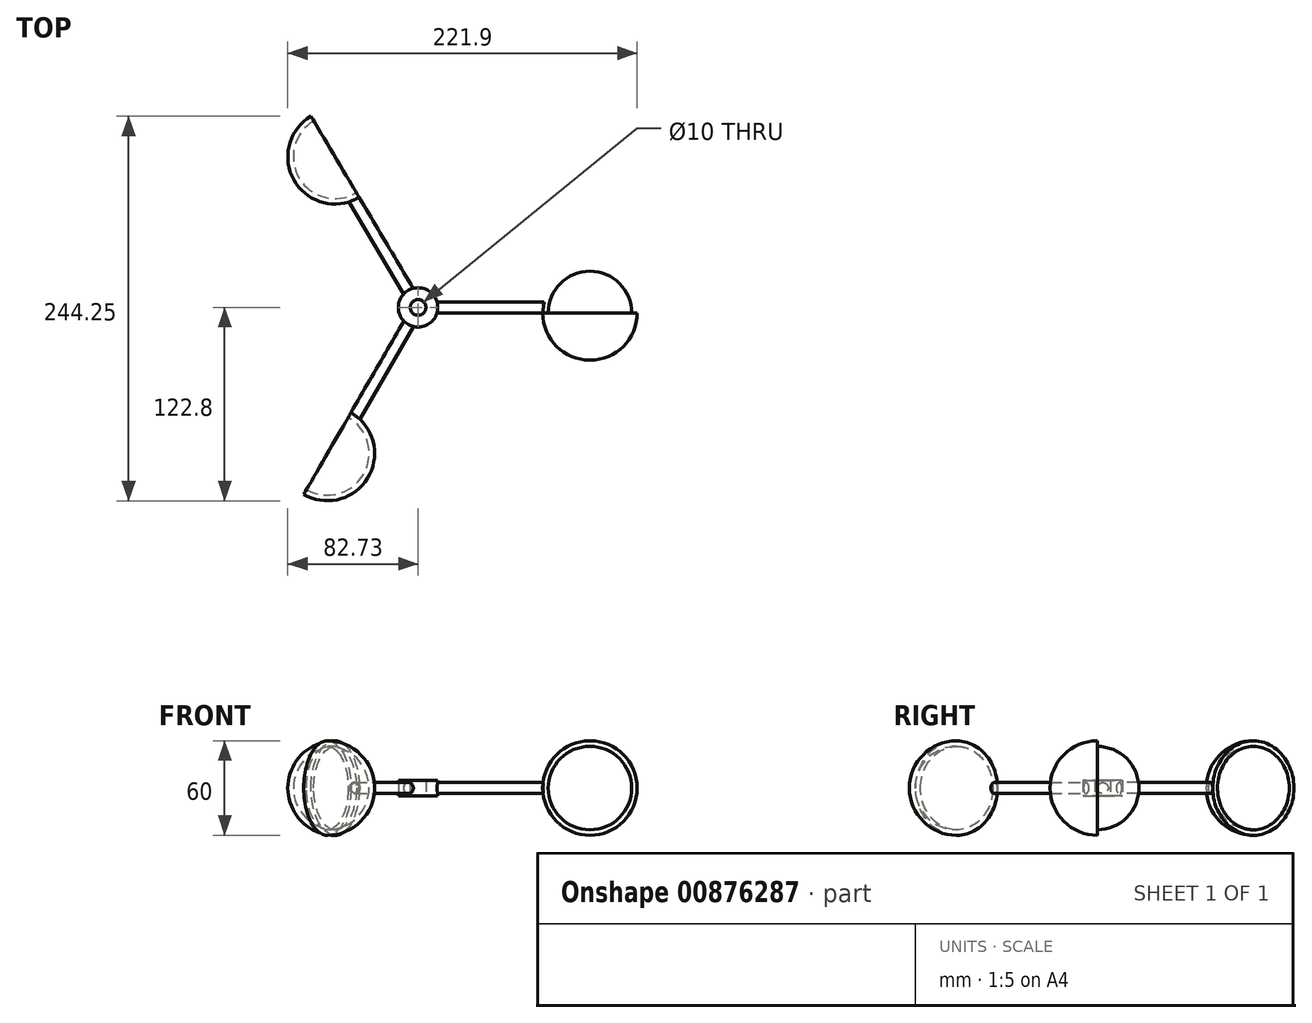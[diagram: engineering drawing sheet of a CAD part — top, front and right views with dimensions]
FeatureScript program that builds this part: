
annotation { "Feature Type Name" : "Feature", "Feature Type Description" : "" }
export const myFeature = defineFeature(function(context is Context, id is Id, definition is map)
    precondition{}
    {
        {
            var Q0;
            Q0=qCreatedBy(makeId("Top.planeOp"),FACE);
            var sketch = newSketch(context, id + "F0", { "sketchPlane" : qUnion([Q0])});
            skCircle(sketch, "E0", {"center": v(0, 0) * mm, "radius": 12.5 * mm});
            skCircle(sketch, "E1", {"center": v(0, 0) * mm, "radius": 5 * mm});
            skSolve(sketch);
        }
        {
            var Q0;
            Q0=qSketchRegion(id+"F0",true);
            var Q1;
            Q1=sQuery(id+"F0.wireOp",EDGE,"E0");
            extrude(context, id + "F1", {"entities" : qUnion([Q0]), "surfaceEntities" : qUnion([Q1]), "endBound" : BoundingType.SYMMETRIC, "depth" : 10 * mm, "offsetDistance" : 25 * mm});
        }
        {
            var Q0;
            Q0=qCreatedBy(makeId("Top.planeOp"),FACE);
            var sketch = newSketch(context, id + "F2", { "sketchPlane" : qUnion([Q0])});
            skLineSegment(sketch, "E2.bottom", {"start": v(0, -3.5) * mm, "end": v(80, -3.5) * mm});
            skLineSegment(sketch, "E2.top", {"start": v(0, 3.5) * mm, "end": v(80, 3.5) * mm});
            skLineSegment(sketch, "E2.left", {"start": v(0, -3.5) * mm, "end": v(0, 3.5) * mm, "construction": true});
            skLineSegment(sketch, "E2.right", {"start": v(80, -3.5) * mm, "end": v(80, 3.5) * mm});
            skLineSegment(sketch, "E3.0", {"start": v(5, -3.5) * mm, "end": v(5, 3.5) * mm});
            skLineSegment(sketch, "E4", {"start": v(0, 0) * mm, "end": v(80, 0) * mm});
            skSolve(sketch);
        }
        {
            var Q0;
            {var subQ0=sQuery(id+"F2.wireOp",EDGE,"E2.right");var subQ1=sQuery(id+"F2.wireOp",EDGE,"E2.top");var subQ2=makeQuery(id+"F2.imprint","INTERSECT",VERTEX,{"derivedFrom":[subQ1,subQ0]});Q0=makeQuery(id+"F2.imprint","IMPRINT",FACE,{"disambiguationData":[TD([[makeQuery(id+"F2.imprint","IMPRINT",EDGE,{"disambiguationData":[TD([[subQ2,1.0]])],"derivedFrom":subQ1}),-1.0]])]});}
            var Q1;
            Q1=sQuery(id+"F2.wireOp",EDGE,"E4");
            revolve(context, id + "F3", {"operationType" : NewBodyOperationType.ADD, "surfaceOperationType" : NewSurfaceOperationType.NEW, "entities" : qUnion([Q0]), "axis" : qUnion([Q1]), "revolveType" : RevolveType.FULL});
        }
        {
            var Q0;
            Q0=qCreatedBy(makeId("Top.planeOp"),FACE);
            var sketch = newSketch(context, id + "F4", { "sketchPlane" : qUnion([Q0])});
            skLineSegment(sketch, "E5.bottom", {"start": v(3, 1.79) * mm, "end": v(-37.83, 70.58) * mm});
            skLineSegment(sketch, "E5.top", {"start": v(-3, -1.79) * mm, "end": v(-43.85, 67) * mm});
            skLineSegment(sketch, "E5.left", {"start": v(3, 1.79) * mm, "end": v(-3, -1.79) * mm, "construction": true});
            skLineSegment(sketch, "E5.right", {"start": v(-37.83, 70.58) * mm, "end": v(-43.85, 67) * mm});
            skLineSegment(sketch, "E6.0", {"start": v(0.46, 6.09) * mm, "end": v(-5.56, 2.51) * mm});
            skLineSegment(sketch, "E7", {"start": v(0, 0) * mm, "end": v(-40.84, 68.79) * mm});
            skSolve(sketch);
        }
        {
            var Q0;
            {var subQ0=sQuery(id+"F4.wireOp",EDGE,"E5.right");var subQ1=sQuery(id+"F4.wireOp",EDGE,"E5.top");var subQ2=makeQuery(id+"F4.imprint","INTERSECT",VERTEX,{"derivedFrom":[subQ1,subQ0]});Q0=makeQuery(id+"F4.imprint","IMPRINT",FACE,{"disambiguationData":[TD([[makeQuery(id+"F4.imprint","IMPRINT",EDGE,{"disambiguationData":[TD([[subQ2,1.0]])],"derivedFrom":subQ1}),-1.0]])]});}
            var Q1;
            Q1=sQuery(id+"F4.wireOp",EDGE,"E7");
            revolve(context, id + "F5", {"operationType" : NewBodyOperationType.ADD, "surfaceOperationType" : NewSurfaceOperationType.NEW, "entities" : qUnion([Q0]), "axis" : qUnion([Q1]), "revolveType" : RevolveType.FULL});
        }
        {
            var Q0;
            Q0=qCreatedBy(makeId("Top.planeOp"),FACE);
            var sketch = newSketch(context, id + "F6", { "sketchPlane" : qUnion([Q0])});
            skLineSegment(sketch, "E8.bottom", {"start": v(-3.03, 1.75) * mm, "end": v(-43.03, -67.53) * mm});
            skLineSegment(sketch, "E8.top", {"start": v(3.03, -1.75) * mm, "end": v(-36.97, -71.03) * mm});
            skLineSegment(sketch, "E8.left", {"start": v(-3.03, 1.75) * mm, "end": v(3.03, -1.75) * mm, "construction": true});
            skLineSegment(sketch, "E8.right", {"start": v(-43.03, -67.53) * mm, "end": v(-36.97, -71.03) * mm});
            skLineSegment(sketch, "E9.0", {"start": v(-5.53, -2.58) * mm, "end": v(0.53, -6.08) * mm});
            skLineSegment(sketch, "E10", {"start": v(0, 0) * mm, "end": v(-40, -69.28) * mm});
            skSolve(sketch);
        }
        {
            var Q0;
            {var subQ0=sQuery(id+"F6.wireOp",EDGE,"E8.right");var subQ1=sQuery(id+"F6.wireOp",EDGE,"E8.top");var subQ2=makeQuery(id+"F6.imprint","INTERSECT",VERTEX,{"derivedFrom":[subQ1,subQ0]});Q0=makeQuery(id+"F6.imprint","IMPRINT",FACE,{"disambiguationData":[TD([[makeQuery(id+"F6.imprint","IMPRINT",EDGE,{"disambiguationData":[TD([[subQ2,1.0]])],"derivedFrom":subQ1}),-1.0]])]});}
            var Q1;
            Q1=sQuery(id+"F6.wireOp",EDGE,"E10");
            revolve(context, id + "F7", {"operationType" : NewBodyOperationType.ADD, "surfaceOperationType" : NewSurfaceOperationType.NEW, "entities" : qUnion([Q0]), "axis" : qUnion([Q1]), "revolveType" : RevolveType.FULL});
        }
        {
            var Q0;
            Q0=qCreatedBy(makeId("Top.planeOp"),FACE);
            var sketch = newSketch(context, id + "F8", { "sketchPlane" : qUnion([Q0])});
            skLineSegment(sketch, "E11", {"start": v(0, -3.5) * mm, "end": v(146.58, -3.5) * mm});
            skLineSegment(sketch, "E12", {"start": v(3, 1.79) * mm, "end": v(-72.02, 128.16) * mm});
            skLineSegment(sketch, "E13", {"start": v(-3.03, 1.75) * mm, "end": v(-75.24, -123.32) * mm});
            skArc(sketch, "E14", {"start": v(-68.04, 121.45) * mm, "mid": v(-78.52, 80.34) * mm, "end": v(-37.41, 69.86) * mm});
            skArc(sketch, "E15", {"start": v(-72.62, -118.78) * mm, "mid": v(-31.64, -107.8) * mm, "end": v(-42.62, -66.81) * mm});
            skArc(sketch, "E16", {"start": v(139.17, -3.5) * mm, "mid": v(109.17, 26.5) * mm, "end": v(79.17, -3.5) * mm});
            skArc(sketch, "E17.0", {"start": v(135.67, -3.5) * mm, "mid": v(109.17, 23) * mm, "end": v(82.67, -3.5) * mm});
            skArc(sketch, "E18.0", {"start": v(-70.87, -115.75) * mm, "mid": v(-34.67, -106.05) * mm, "end": v(-44.37, -69.85) * mm});
            skArc(sketch, "E19.0", {"start": v(-66.26, 118.45) * mm, "mid": v(-75.51, 82.13) * mm, "end": v(-39.2, 72.87) * mm});
            skSolve(sketch);
        }
        {
            var Q0;
            {var subQ0=sQuery(id+"F8.wireOp",EDGE,"E16");Q0=makeQuery(id+"F8.imprint","IMPRINT",FACE,{"disambiguationData":[TD([[makeQuery(id+"F8.imprint","IMPRINT",EDGE,{"derivedFrom":subQ0}),1.0]])]});}
            var Q1;
            Q1=sQuery(id+"F8.wireOp",EDGE,"E11");
            revolve(context, id + "F9", {"operationType" : NewBodyOperationType.ADD, "surfaceOperationType" : NewSurfaceOperationType.NEW, "entities" : qUnion([Q0]), "axis" : qUnion([Q1]), "revolveType" : RevolveType.SYMMETRIC, "angle" : 180 * degree});
        }
        {
            var Q0;
            {var subQ0=sQuery(id+"F8.wireOp",EDGE,"E14");Q0=makeQuery(id+"F8.imprint","IMPRINT",FACE,{"disambiguationData":[TD([[makeQuery(id+"F8.imprint","IMPRINT",EDGE,{"derivedFrom":subQ0}),1.0]])]});}
            var Q1;
            Q1=sQuery(id+"F8.wireOp",EDGE,"E12");
            revolve(context, id + "F10", {"operationType" : NewBodyOperationType.ADD, "surfaceOperationType" : NewSurfaceOperationType.NEW, "entities" : qUnion([Q0]), "axis" : qUnion([Q1]), "revolveType" : RevolveType.SYMMETRIC, "angle" : 180 * degree});
        }
        {
            var Q0;
            {var subQ0=sQuery(id+"F8.wireOp",EDGE,"E15");Q0=makeQuery(id+"F8.imprint","IMPRINT",FACE,{"disambiguationData":[TD([[makeQuery(id+"F8.imprint","IMPRINT",EDGE,{"derivedFrom":subQ0}),1.0]])]});}
            var Q1;
            Q1=sQuery(id+"F8.wireOp",EDGE,"E13");
            revolve(context, id + "F11", {"operationType" : NewBodyOperationType.ADD, "surfaceOperationType" : NewSurfaceOperationType.NEW, "entities" : qUnion([Q0]), "axis" : qUnion([Q1]), "revolveType" : RevolveType.SYMMETRIC, "angle" : 180 * degree});
        }
    });
